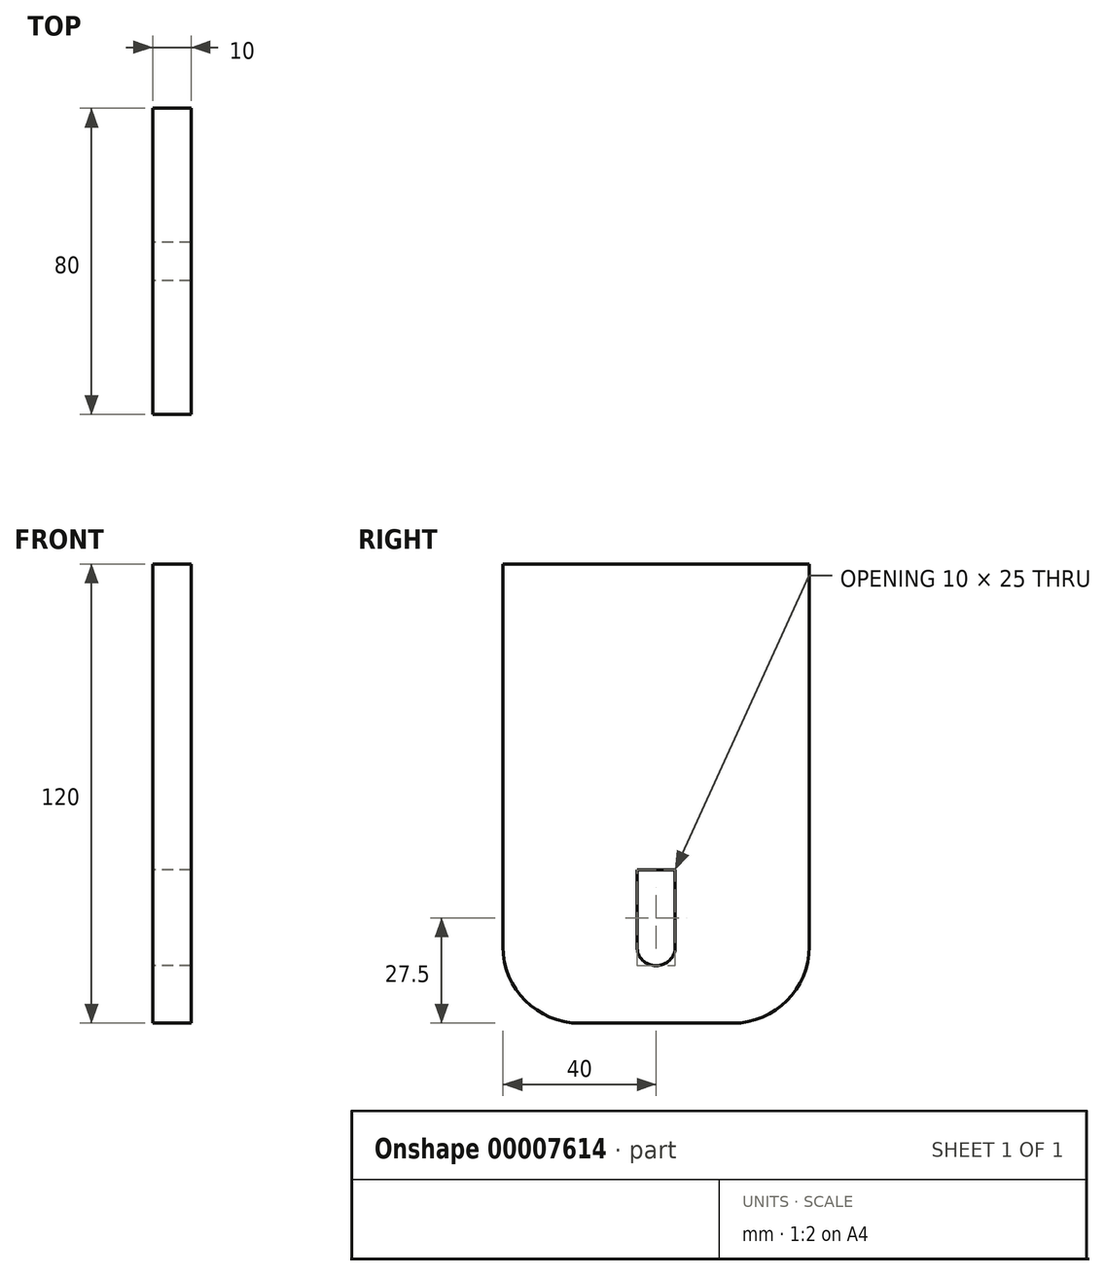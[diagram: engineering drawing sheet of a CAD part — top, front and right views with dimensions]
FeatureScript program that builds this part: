
annotation { "Feature Type Name" : "Feature", "Feature Type Description" : "" }
export const myFeature = defineFeature(function(context is Context, id is Id, definition is map)
    precondition{}
    {
        {
            var Q0;
            Q0=qCreatedBy(makeId("Right.planeOp"),FACE);
            var sketch = newSketch(context, id + "F0", { "sketchPlane" : qUnion([Q0])});
            skLineSegment(sketch, "E0", {"start": v(-5, 20) * mm, "end": v(5, 20) * mm});
            skLineSegment(sketch, "E1", {"start": v(5, 20) * mm, "end": v(5, 0) * mm});
            skArc(sketch, "E2", {"start": v(5, 0) * mm, "mid": v(0, -5) * mm, "end": v(-5, 0) * mm});
            skLineSegment(sketch, "E3", {"start": v(-5, 0) * mm, "end": v(-5, 20) * mm});
            skLineSegment(sketch, "E4", {"start": v(40, 100) * mm, "end": v(-40, 100) * mm});
            skLineSegment(sketch, "E5", {"start": v(-40, 100) * mm, "end": v(-40, 0) * mm});
            skLineSegment(sketch, "E6", {"start": v(-20, -20) * mm, "end": v(20, -20) * mm});
            skLineSegment(sketch, "E7", {"start": v(40, 0) * mm, "end": v(40, 100) * mm});
            skPoint(sketch, "E8.visualSharp", {"position": v(-40, -20) * mm});
            skArc(sketch, "E8.filletArc", {"start": v(-40, 0) * mm, "mid": v(-34.14, -14.14) * mm, "end": v(-20, -20) * mm});
            skPoint(sketch, "E9.visualSharp", {"position": v(40, -20) * mm});
            skArc(sketch, "E9.filletArc", {"start": v(20, -20) * mm, "mid": v(34.14, -14.14) * mm, "end": v(40, 0) * mm});
            skSolve(sketch);
        }
        {
            var Q0;
            Q0 = qSketchRegion(id + "F0", true);
            extrude(context, id + "F1", {"entities" : qUnion([Q0]), "endBound" : BoundingType.SYMMETRIC, "depth" : 10 * mm});
        }
    });
